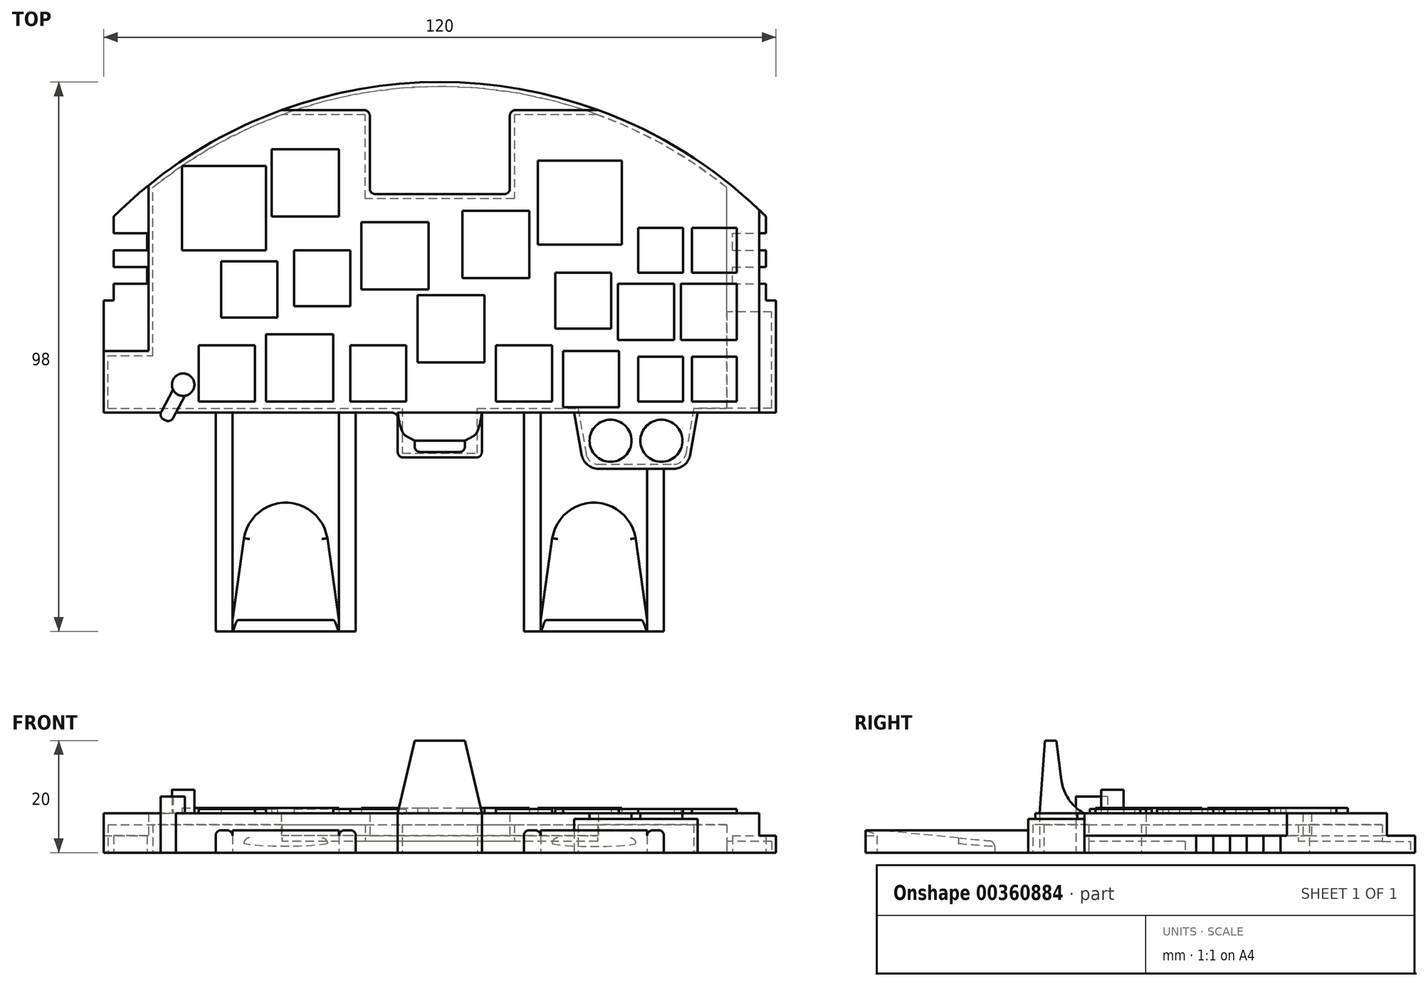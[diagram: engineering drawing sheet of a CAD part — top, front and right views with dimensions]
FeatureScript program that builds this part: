
annotation { "Feature Type Name" : "Feature", "Feature Type Description" : "" }
export const myFeature = defineFeature(function(context is Context, id is Id, definition is map)
    precondition{}
    {
        {
            var Q0;
            Q0=qCreatedBy(makeId("Top.planeOp"),FACE);
            var sketch = newSketch(context, id + "F0", { "sketchPlane" : qUnion([Q0])});
            skLineSegment(sketch, "E0", {"start": v(-60, 0) * mm, "end": v(60, 0) * mm});
            skLineSegment(sketch, "E1", {"start": v(60, 0) * mm, "end": v(60, 20) * mm});
            skLineSegment(sketch, "E2", {"start": v(60, 20) * mm, "end": v(58.2, 20) * mm});
            skLineSegment(sketch, "E3", {"start": v(58.2, 20) * mm, "end": v(58.2, 35) * mm});
            skLineSegment(sketch, "E4", {"start": v(-60, 0) * mm, "end": v(-60, 20) * mm});
            skLineSegment(sketch, "E5", {"start": v(-60, 20) * mm, "end": v(-58.2, 20) * mm});
            skLineSegment(sketch, "E6", {"start": v(-58.2, 20) * mm, "end": v(-58.2, 35) * mm});
            skArc(sketch, "E7", {"start": v(58.2, 35) * mm, "mid": v(0, 59) * mm, "end": v(-58.2, 35) * mm});
            skPoint(sketch, "E8", {"position": v(0, 0) * mm});
            skPoint(sketch, "E9", {"position": v(0, 59) * mm});
            skSolve(sketch);
        }
        {
            var Q0;
            Q0 = qSketchRegion(id + "F0", true);
            extrude(context, id + "F1", {"entities" : qUnion([Q0]), "depth" : 3 * mm});
        }
        {
            var Q0;
            Q0=makeQuery(id+"F1.opExtrude","CAP_FACE",FACE,{"disambiguationData":[OSD([sQuery(id+"F0.wireOp",EDGE,"E0"),sQuery(id+"F0.wireOp",EDGE,"E1"),sQuery(id+"F0.wireOp",EDGE,"E2"),sQuery(id+"F0.wireOp",EDGE,"E3"),sQuery(id+"F0.wireOp",EDGE,"E4"),sQuery(id+"F0.wireOp",EDGE,"E5"),sQuery(id+"F0.wireOp",EDGE,"E6"),sQuery(id+"F0.wireOp",EDGE,"E7")])],"isStart":false});
            var sketch = newSketch(context, id + "F2", { "sketchPlane" : qUnion([Q0])});
            skLineSegment(sketch, "E10", {"start": v(-60, 0) * mm, "end": v(57, 0) * mm});
            skLineSegment(sketch, "E11", {"start": v(57, 0) * mm, "end": v(57, 36.17) * mm});
            skLineSegment(sketch, "E12", {"start": v(-60, 0) * mm, "end": v(-60, 11) * mm});
            skLineSegment(sketch, "E13", {"start": v(-60, 11) * mm, "end": v(-52, 11) * mm});
            skLineSegment(sketch, "E14", {"start": v(-52, 11) * mm, "end": v(-52, 40.57) * mm});
            skArc(sketch, "E15", {"start": v(57, 36.17) * mm, "mid": v(43.57, 46.57) * mm, "end": v(28.3, 54) * mm});
            skLineSegment(sketch, "E16", {"start": v(-12.5, 39) * mm, "end": v(12.5, 39) * mm});
            skLineSegment(sketch, "E17", {"start": v(12.5, 39) * mm, "end": v(12.5, 54) * mm});
            skLineSegment(sketch, "E18", {"start": v(-12.5, 39) * mm, "end": v(-12.5, 54) * mm});
            skPoint(sketch, "E19", {"position": v(0, 39) * mm});
            skLineSegment(sketch, "E20", {"start": v(12.5, 54) * mm, "end": v(28.3, 54) * mm});
            skLineSegment(sketch, "E21", {"start": v(-12.5, 54) * mm, "end": v(-28.3, 54) * mm});
            skArc(sketch, "E22.trimOffspring", {"start": v(-28.3, 54) * mm, "mid": v(-40.7, 48.27) * mm, "end": v(-52, 40.57) * mm});
            skSolve(sketch);
        }
        {
            var Q0;
            Q0 = qSketchRegion(id + "F2", true);
            extrude(context, id + "F3", {"entities" : qUnion([Q0]), "operationType" : NewBodyOperationType.ADD, "depth" : 4 * mm});
        }
        {
            var Q0;
            Q0=makeQuery(id+"F3.opExtrude","CAP_FACE",FACE,{"disambiguationData":[OSD([sQuery(id+"F2.wireOp",EDGE,"E10"),sQuery(id+"F2.wireOp",EDGE,"E11"),sQuery(id+"F2.wireOp",EDGE,"E12"),sQuery(id+"F2.wireOp",EDGE,"E13"),sQuery(id+"F2.wireOp",EDGE,"E14"),sQuery(id+"F2.wireOp",EDGE,"E15"),sQuery(id+"F2.wireOp",EDGE,"E16"),sQuery(id+"F2.wireOp",EDGE,"E17"),sQuery(id+"F2.wireOp",EDGE,"E18"),sQuery(id+"F2.wireOp",EDGE,"E20"),sQuery(id+"F2.wireOp",EDGE,"E21"),sQuery(id+"F2.wireOp",EDGE,"E22.trimOffspring")])],"isStart":false});
            var sketch = newSketch(context, id + "F4", { "sketchPlane" : qUnion([Q0])});
            skLineSegment(sketch, "E23.bottom", {"start": v(17.5, 45) * mm, "end": v(32.5, 45) * mm});
            skLineSegment(sketch, "E23.top", {"start": v(17.5, 30) * mm, "end": v(32.5, 30) * mm});
            skLineSegment(sketch, "E23.left", {"start": v(17.5, 45) * mm, "end": v(17.5, 30) * mm});
            skLineSegment(sketch, "E23.right", {"start": v(32.5, 45) * mm, "end": v(32.5, 30) * mm});
            skLineSegment(sketch, "E24.bottom", {"start": v(-46, 44) * mm, "end": v(-31, 44) * mm});
            skLineSegment(sketch, "E24.top", {"start": v(-46, 29) * mm, "end": v(-31, 29) * mm});
            skLineSegment(sketch, "E24.left", {"start": v(-46, 44) * mm, "end": v(-46, 29) * mm});
            skLineSegment(sketch, "E24.right", {"start": v(-31, 44) * mm, "end": v(-31, 29) * mm});
            skSolve(sketch);
        }
        {
            var Q0;
            Q0 = qSketchRegion(id + "F4", true);
            extrude(context, id + "F5", {"entities" : qUnion([Q0]), "operationType" : NewBodyOperationType.ADD, "depth" : 1 * mm});
        }
        {
            var Q0;
            Q0=makeQuery(id+"F3.opExtrude","CAP_FACE",FACE,{"disambiguationData":[OSD([sQuery(id+"F2.wireOp",EDGE,"E10"),sQuery(id+"F2.wireOp",EDGE,"E11"),sQuery(id+"F2.wireOp",EDGE,"E12"),sQuery(id+"F2.wireOp",EDGE,"E13"),sQuery(id+"F2.wireOp",EDGE,"E14"),sQuery(id+"F2.wireOp",EDGE,"E15"),sQuery(id+"F2.wireOp",EDGE,"E16"),sQuery(id+"F2.wireOp",EDGE,"E17"),sQuery(id+"F2.wireOp",EDGE,"E18"),sQuery(id+"F2.wireOp",EDGE,"E20"),sQuery(id+"F2.wireOp",EDGE,"E21"),sQuery(id+"F2.wireOp",EDGE,"E22.trimOffspring")])],"isStart":false});
            var sketch = newSketch(context, id + "F6", { "sketchPlane" : qUnion([Q0])});
            skLineSegment(sketch, "E25.bottom", {"start": v(-30, 47) * mm, "end": v(-18, 47) * mm});
            skLineSegment(sketch, "E25.top", {"start": v(-30, 35) * mm, "end": v(-18, 35) * mm});
            skLineSegment(sketch, "E25.left", {"start": v(-30, 47) * mm, "end": v(-30, 35) * mm});
            skLineSegment(sketch, "E25.right", {"start": v(-18, 47) * mm, "end": v(-18, 35) * mm});
            skLineSegment(sketch, "E26.bottom", {"start": v(-14, 34) * mm, "end": v(-2, 34) * mm});
            skLineSegment(sketch, "E26.top", {"start": v(-14, 22) * mm, "end": v(-2, 22) * mm});
            skLineSegment(sketch, "E26.left", {"start": v(-14, 34) * mm, "end": v(-14, 22) * mm});
            skLineSegment(sketch, "E26.right", {"start": v(-2, 34) * mm, "end": v(-2, 22) * mm});
            skLineSegment(sketch, "E27.bottom", {"start": v(4, 36) * mm, "end": v(16, 36) * mm});
            skLineSegment(sketch, "E27.top", {"start": v(4, 24) * mm, "end": v(16, 24) * mm});
            skLineSegment(sketch, "E27.left", {"start": v(4, 36) * mm, "end": v(4, 24) * mm});
            skLineSegment(sketch, "E27.right", {"start": v(16, 36) * mm, "end": v(16, 24) * mm});
            skLineSegment(sketch, "E28.bottom", {"start": v(-4, 21) * mm, "end": v(8, 21) * mm});
            skLineSegment(sketch, "E28.top", {"start": v(-4, 9) * mm, "end": v(8, 9) * mm});
            skLineSegment(sketch, "E28.left", {"start": v(-4, 21) * mm, "end": v(-4, 9) * mm});
            skLineSegment(sketch, "E28.right", {"start": v(8, 21) * mm, "end": v(8, 9) * mm});
            skLineSegment(sketch, "E29.bottom", {"start": v(-31, 14) * mm, "end": v(-19, 14) * mm});
            skLineSegment(sketch, "E29.top", {"start": v(-31, 2) * mm, "end": v(-19, 2) * mm});
            skLineSegment(sketch, "E29.left", {"start": v(-31, 14) * mm, "end": v(-31, 2) * mm});
            skLineSegment(sketch, "E29.right", {"start": v(-19, 14) * mm, "end": v(-19, 2) * mm});
            skSolve(sketch);
        }
        {
            var Q0;
            Q0 = qSketchRegion(id + "F6", true);
            extrude(context, id + "F7", {"entities" : qUnion([Q0]), "operationType" : NewBodyOperationType.ADD, "depth" : 1 * mm});
        }
        {
            var Q0;
            Q0=makeQuery(id+"F3.opExtrude","CAP_FACE",FACE,{"disambiguationData":[OSD([sQuery(id+"F2.wireOp",EDGE,"E10"),sQuery(id+"F2.wireOp",EDGE,"E11"),sQuery(id+"F2.wireOp",EDGE,"E12"),sQuery(id+"F2.wireOp",EDGE,"E13"),sQuery(id+"F2.wireOp",EDGE,"E14"),sQuery(id+"F2.wireOp",EDGE,"E15"),sQuery(id+"F2.wireOp",EDGE,"E16"),sQuery(id+"F2.wireOp",EDGE,"E17"),sQuery(id+"F2.wireOp",EDGE,"E18"),sQuery(id+"F2.wireOp",EDGE,"E20"),sQuery(id+"F2.wireOp",EDGE,"E21"),sQuery(id+"F2.wireOp",EDGE,"E22.trimOffspring")])],"isStart":false});
            var sketch = newSketch(context, id + "F8", { "sketchPlane" : qUnion([Q0])});
            skLineSegment(sketch, "E30.bottom", {"start": v(-39, 27) * mm, "end": v(-29, 27) * mm});
            skLineSegment(sketch, "E30.top", {"start": v(-39, 17) * mm, "end": v(-29, 17) * mm});
            skLineSegment(sketch, "E30.left", {"start": v(-39, 27) * mm, "end": v(-39, 17) * mm});
            skLineSegment(sketch, "E30.right", {"start": v(-29, 27) * mm, "end": v(-29, 17) * mm});
            skLineSegment(sketch, "E31.bottom", {"start": v(-26, 29) * mm, "end": v(-16, 29) * mm});
            skLineSegment(sketch, "E31.top", {"start": v(-26, 19) * mm, "end": v(-16, 19) * mm});
            skLineSegment(sketch, "E31.left", {"start": v(-26, 29) * mm, "end": v(-26, 19) * mm});
            skLineSegment(sketch, "E31.right", {"start": v(-16, 29) * mm, "end": v(-16, 19) * mm});
            skLineSegment(sketch, "E32.bottom", {"start": v(-16, 12) * mm, "end": v(-6, 12) * mm});
            skLineSegment(sketch, "E32.top", {"start": v(-16, 2) * mm, "end": v(-6, 2) * mm});
            skLineSegment(sketch, "E32.left", {"start": v(-16, 12) * mm, "end": v(-16, 2) * mm});
            skLineSegment(sketch, "E32.right", {"start": v(-6, 12) * mm, "end": v(-6, 2) * mm});
            skLineSegment(sketch, "E33.bottom", {"start": v(10, 12) * mm, "end": v(20, 12) * mm});
            skLineSegment(sketch, "E33.top", {"start": v(10, 2) * mm, "end": v(20, 2) * mm});
            skLineSegment(sketch, "E33.left", {"start": v(10, 12) * mm, "end": v(10, 2) * mm});
            skLineSegment(sketch, "E33.right", {"start": v(20, 12) * mm, "end": v(20, 2) * mm});
            skLineSegment(sketch, "E34.bottom", {"start": v(22, 11) * mm, "end": v(32, 11) * mm});
            skLineSegment(sketch, "E34.top", {"start": v(22, 1) * mm, "end": v(32, 1) * mm});
            skLineSegment(sketch, "E34.left", {"start": v(22, 11) * mm, "end": v(22, 1) * mm});
            skLineSegment(sketch, "E34.right", {"start": v(32, 11) * mm, "end": v(32, 1) * mm});
            skLineSegment(sketch, "E35.bottom", {"start": v(20.6, 25) * mm, "end": v(30.6, 25) * mm});
            skLineSegment(sketch, "E35.top", {"start": v(20.6, 15) * mm, "end": v(30.6, 15) * mm});
            skLineSegment(sketch, "E35.left", {"start": v(20.6, 25) * mm, "end": v(20.6, 15) * mm});
            skLineSegment(sketch, "E35.right", {"start": v(30.6, 25) * mm, "end": v(30.6, 15) * mm});
            skLineSegment(sketch, "E36.bottom", {"start": v(31.8, 23) * mm, "end": v(41.8, 23) * mm});
            skLineSegment(sketch, "E36.top", {"start": v(31.8, 13) * mm, "end": v(41.8, 13) * mm});
            skLineSegment(sketch, "E36.left", {"start": v(31.8, 23) * mm, "end": v(31.8, 13) * mm});
            skLineSegment(sketch, "E36.right", {"start": v(41.8, 23) * mm, "end": v(41.8, 13) * mm});
            skLineSegment(sketch, "E37.bottom", {"start": v(43, 23) * mm, "end": v(53, 23) * mm});
            skLineSegment(sketch, "E37.top", {"start": v(43, 13) * mm, "end": v(53, 13) * mm});
            skLineSegment(sketch, "E37.left", {"start": v(43, 23) * mm, "end": v(43, 13) * mm});
            skLineSegment(sketch, "E37.right", {"start": v(53, 23) * mm, "end": v(53, 13) * mm});
            skLineSegment(sketch, "E38.bottom", {"start": v(-43, 12) * mm, "end": v(-33, 12) * mm});
            skLineSegment(sketch, "E38.top", {"start": v(-43, 2) * mm, "end": v(-33, 2) * mm});
            skLineSegment(sketch, "E38.left", {"start": v(-43, 12) * mm, "end": v(-43, 2) * mm});
            skLineSegment(sketch, "E38.right", {"start": v(-33, 12) * mm, "end": v(-33, 2) * mm});
            skSolve(sketch);
        }
        {
            var Q0;
            Q0 = qSketchRegion(id + "F8", true);
            extrude(context, id + "F9", {"entities" : qUnion([Q0]), "operationType" : NewBodyOperationType.ADD, "depth" : 0.8 * mm});
        }
        {
            var Q0;
            Q0=makeQuery(id+"F3.opExtrude","CAP_FACE",FACE,{"disambiguationData":[OSD([sQuery(id+"F2.wireOp",EDGE,"E10"),sQuery(id+"F2.wireOp",EDGE,"E11"),sQuery(id+"F2.wireOp",EDGE,"E12"),sQuery(id+"F2.wireOp",EDGE,"E13"),sQuery(id+"F2.wireOp",EDGE,"E14"),sQuery(id+"F2.wireOp",EDGE,"E15"),sQuery(id+"F2.wireOp",EDGE,"E16"),sQuery(id+"F2.wireOp",EDGE,"E17"),sQuery(id+"F2.wireOp",EDGE,"E18"),sQuery(id+"F2.wireOp",EDGE,"E20"),sQuery(id+"F2.wireOp",EDGE,"E21"),sQuery(id+"F2.wireOp",EDGE,"E22.trimOffspring")])],"isStart":false});
            var sketch = newSketch(context, id + "F10", { "sketchPlane" : qUnion([Q0])});
            skLineSegment(sketch, "E39.bottom", {"start": v(35.4, 10) * mm, "end": v(43.4, 10) * mm});
            skLineSegment(sketch, "E39.top", {"start": v(35.4, 2) * mm, "end": v(43.4, 2) * mm});
            skLineSegment(sketch, "E39.left", {"start": v(35.4, 10) * mm, "end": v(35.4, 2) * mm});
            skLineSegment(sketch, "E39.right", {"start": v(43.4, 10) * mm, "end": v(43.4, 2) * mm});
            skLineSegment(sketch, "E40.bottom", {"start": v(45, 10) * mm, "end": v(53, 10) * mm});
            skLineSegment(sketch, "E40.top", {"start": v(45, 2) * mm, "end": v(53, 2) * mm});
            skLineSegment(sketch, "E40.left", {"start": v(45, 10) * mm, "end": v(45, 2) * mm});
            skLineSegment(sketch, "E40.right", {"start": v(53, 10) * mm, "end": v(53, 2) * mm});
            skLineSegment(sketch, "E41.bottom", {"start": v(35.4, 33) * mm, "end": v(43.4, 33) * mm});
            skLineSegment(sketch, "E41.top", {"start": v(35.4, 25) * mm, "end": v(43.4, 25) * mm});
            skLineSegment(sketch, "E41.left", {"start": v(35.4, 33) * mm, "end": v(35.4, 25) * mm});
            skLineSegment(sketch, "E41.right", {"start": v(43.4, 33) * mm, "end": v(43.4, 25) * mm});
            skLineSegment(sketch, "E42.bottom", {"start": v(45, 33) * mm, "end": v(53, 33) * mm});
            skLineSegment(sketch, "E42.top", {"start": v(45, 25) * mm, "end": v(53, 25) * mm});
            skLineSegment(sketch, "E42.left", {"start": v(45, 33) * mm, "end": v(45, 25) * mm});
            skLineSegment(sketch, "E42.right", {"start": v(53, 33) * mm, "end": v(53, 25) * mm});
            skSolve(sketch);
        }
        {
            var Q0;
            Q0 = qSketchRegion(id + "F10", true);
            extrude(context, id + "F11", {"entities" : qUnion([Q0]), "operationType" : NewBodyOperationType.ADD, "depth" : 0.8 * mm});
        }
        {
            var Q0;
            Q0=qCreatedBy(makeId("Top.planeOp"),FACE);
            var sketch = newSketch(context, id + "F12", { "sketchPlane" : qUnion([Q0])});
            skCircle(sketch, "E43", {"center": v(-45.8, 5) * mm, "radius": 2 * mm});
            skLineSegment(sketch, "E44", {"start": v(-47.61, 4.15) * mm, "end": v(-50.19, -0.7) * mm});
            skLineSegment(sketch, "E45", {"start": v(-50.19, -0.7) * mm, "end": v(-48.07, -1.83) * mm});
            skLineSegment(sketch, "E46", {"start": v(-48.07, -1.83) * mm, "end": v(-45.5, 3.02) * mm});
            skSolve(sketch);
        }
        {
            var Q0;
            Q0 = qSketchRegion(id + "F12", true);
            extrude(context, id + "F13", {"entities" : qUnion([Q0]), "operationType" : NewBodyOperationType.ADD, "depth" : 10 * mm});
        }
        {
            var Q0;
            Q0=makeQuery(id+"F13.opExtrude","CAP_FACE",FACE,{"disambiguationData":[OSD([sQuery(id+"F12.wireOp",EDGE,"E43"),sQuery(id+"F12.wireOp",EDGE,"E44"),sQuery(id+"F12.wireOp",EDGE,"E45"),sQuery(id+"F12.wireOp",EDGE,"E46")])],"isStart":false});
            var sketch = newSketch(context, id + "F14", { "sketchPlane" : qUnion([Q0])});
            skCircle(sketch, "E47", {"center": v(-45.8, 5) * mm, "radius": 2 * mm});
            skSolve(sketch);
        }
        {
            var Q0;
            Q0 = qSketchRegion(id + "F14", true);
            extrude(context, id + "F15", {"entities" : qUnion([Q0]), "operationType" : NewBodyOperationType.ADD, "depth" : 1.2 * mm});
        }
        {
            var Q0;
            Q0=qCreatedBy(makeId("Top.planeOp"),FACE);
            var sketch = newSketch(context, id + "F16", { "sketchPlane" : qUnion([Q0])});
            skLineSegment(sketch, "E48", {"start": v(44.67, -7.52) * mm, "end": v(46, 0) * mm});
            skLineSegment(sketch, "E49", {"start": v(25.33, -7.52) * mm, "end": v(24, 0) * mm});
            skLineSegment(sketch, "E50", {"start": v(28.28, -10) * mm, "end": v(41.72, -10) * mm});
            skArc(sketch, "E51", {"start": v(25.33, -7.52) * mm, "mid": v(26.35, -9.3) * mm, "end": v(28.28, -10) * mm});
            skArc(sketch, "E52", {"start": v(44.67, -7.52) * mm, "mid": v(43.65, -9.3) * mm, "end": v(41.72, -10) * mm});
            skLineSegment(sketch, "E53", {"start": v(24, 0) * mm, "end": v(46, 0) * mm});
            skCircle(sketch, "E54", {"center": v(30.47, -5) * mm, "radius": 3.75 * mm});
            skCircle(sketch, "E55", {"center": v(39.53, -5) * mm, "radius": 3.75 * mm});
            skSolve(sketch);
        }
        {
            var Q0;
            Q0 = qSketchRegion(id + "F16", true);
            var Q1;
            Q1=makeQuery(id+"F16.imprint","IMPRINT",FACE,{"disambiguationData":[TD([[makeQuery(id+"F16.imprint","IMPRINT",EDGE,{"derivedFrom":sQuery(id+"F16.wireOp",EDGE,"E54")}),1.0]])]});
            var Q2;
            Q2=makeQuery(id+"F16.imprint","IMPRINT",FACE,{"disambiguationData":[TD([[makeQuery(id+"F16.imprint","IMPRINT",EDGE,{"derivedFrom":sQuery(id+"F16.wireOp",EDGE,"E55")}),1.0]])]});
            extrude(context, id + "F17", {"entities" : qUnion([Q0, Q1, Q2]), "operationType" : NewBodyOperationType.ADD, "depth" : 6 * mm});
        }
        {
            var Q0;
            Q0=qCreatedBy(makeId("Front.planeOp"),FACE);
            var sketch = newSketch(context, id + "F18", { "sketchPlane" : qUnion([Q0])});
            skLineSegment(sketch, "E56.bottom", {"start": v(-40, 4) * mm, "end": v(-37, 4) * mm});
            skLineSegment(sketch, "E56.top", {"start": v(-40, 0) * mm, "end": v(-37, 0) * mm});
            skLineSegment(sketch, "E56.left", {"start": v(-40, 4) * mm, "end": v(-40, 0) * mm});
            skLineSegment(sketch, "E56.right", {"start": v(-37, 4) * mm, "end": v(-37, 0) * mm});
            skLineSegment(sketch, "E57.bottom", {"start": v(-18, 4) * mm, "end": v(-15, 4) * mm});
            skLineSegment(sketch, "E57.top", {"start": v(-18, 0) * mm, "end": v(-15, 0) * mm});
            skLineSegment(sketch, "E57.left", {"start": v(-18, 4) * mm, "end": v(-18, 0) * mm});
            skLineSegment(sketch, "E57.right", {"start": v(-15, 4) * mm, "end": v(-15, 0) * mm});
            skLineSegment(sketch, "E58.bottom", {"start": v(15, 4) * mm, "end": v(18, 4) * mm});
            skLineSegment(sketch, "E58.top", {"start": v(15, 0) * mm, "end": v(18, 0) * mm});
            skLineSegment(sketch, "E58.left", {"start": v(15, 4) * mm, "end": v(15, 0) * mm});
            skLineSegment(sketch, "E58.right", {"start": v(18, 4) * mm, "end": v(18, 0) * mm});
            skLineSegment(sketch, "E59.bottom", {"start": v(37, 4) * mm, "end": v(40, 4) * mm});
            skLineSegment(sketch, "E59.top", {"start": v(37, 0) * mm, "end": v(40, 0) * mm});
            skLineSegment(sketch, "E59.left", {"start": v(37, 4) * mm, "end": v(37, 0) * mm});
            skLineSegment(sketch, "E59.right", {"start": v(40, 4) * mm, "end": v(40, 0) * mm});
            skSolve(sketch);
        }
        {
            var Q0;
            Q0 = qSketchRegion(id + "F18", true);
            extrude(context, id + "F19", {"entities" : qUnion([Q0]), "operationType" : NewBodyOperationType.ADD, "depth" : 39 * mm});
        }
        {
            var Q0;
            Q0=qCreatedBy(makeId("Top.planeOp"),FACE);
            var sketch = newSketch(context, id + "F20", { "sketchPlane" : qUnion([Q0])});
            skLineSegment(sketch, "E60.bottom", {"start": v(-7.5, 0) * mm, "end": v(7.5, 0) * mm});
            skLineSegment(sketch, "E60.top", {"start": v(-7.5, -8) * mm, "end": v(7.5, -8) * mm});
            skLineSegment(sketch, "E60.left", {"start": v(-7.5, 0) * mm, "end": v(-7.5, -8) * mm});
            skLineSegment(sketch, "E60.right", {"start": v(7.5, 0) * mm, "end": v(7.5, -8) * mm});
            skPoint(sketch, "E61", {"position": v(0, -8) * mm});
            skSolve(sketch);
        }
        {
            var Q0;
            Q0 = qSketchRegion(id + "F20", true);
            extrude(context, id + "F21", {"entities" : qUnion([Q0]), "operationType" : NewBodyOperationType.ADD, "depth" : 7 * mm});
        }
        {
            var Q0;
            Q0=qCreatedBy(makeId("Top.planeOp"),FACE);
            cPlane(context, id + "F22", {"entities" : qUnion([Q0]), "cplaneType" : CPlaneType.OFFSET, "offset" : 20 * mm, "width" : 150 * mm, "height" : 150 * mm});
        }
        {
            var Q0;
            Q0=qCreatedBy(id+"F22.planeOp",FACE);
            var sketch = newSketch(context, id + "F23", { "sketchPlane" : qUnion([Q0])});
            skLineSegment(sketch, "E62.bottom", {"start": v(-4.5, -1) * mm, "end": v(4.5, -1) * mm});
            skLineSegment(sketch, "E62.top", {"start": v(-4.5, -7) * mm, "end": v(4.5, -7) * mm});
            skLineSegment(sketch, "E62.left", {"start": v(-4.5, -1) * mm, "end": v(-4.5, -7) * mm});
            skLineSegment(sketch, "E62.right", {"start": v(4.5, -1) * mm, "end": v(4.5, -7) * mm});
            skPoint(sketch, "E63", {"position": v(0, -7) * mm});
            skSolve(sketch);
        }
        {
            var Q0;
            Q0=makeQuery(id+"F21.boolean.opBoolean","MERGE",FACE,{"derivedFrom":[makeQuery(id+"F3.opExtrude","CAP_FACE",FACE,{"disambiguationData":[OSD([sQuery(id+"F2.wireOp",EDGE,"E10"),sQuery(id+"F2.wireOp",EDGE,"E11"),sQuery(id+"F2.wireOp",EDGE,"E12"),sQuery(id+"F2.wireOp",EDGE,"E13"),sQuery(id+"F2.wireOp",EDGE,"E14"),sQuery(id+"F2.wireOp",EDGE,"E15"),sQuery(id+"F2.wireOp",EDGE,"E16"),sQuery(id+"F2.wireOp",EDGE,"E17"),sQuery(id+"F2.wireOp",EDGE,"E18"),sQuery(id+"F2.wireOp",EDGE,"E20"),sQuery(id+"F2.wireOp",EDGE,"E21"),sQuery(id+"F2.wireOp",EDGE,"E22.trimOffspring")])],"isStart":false}),makeQuery(id+"F21.opExtrude","CAP_FACE",FACE,{"disambiguationData":[OSD([sQuery(id+"F20.wireOp",EDGE,"E60.bottom"),sQuery(id+"F20.wireOp",EDGE,"E60.top"),sQuery(id+"F20.wireOp",EDGE,"E60.left"),sQuery(id+"F20.wireOp",EDGE,"E60.right")])],"isStart":false})]});
            var sketch = newSketch(context, id + "F24", { "sketchPlane" : qUnion([Q0])});
            skLineSegment(sketch, "E64.bottom", {"start": v(-7.5, -8) * mm, "end": v(7.5, -8) * mm});
            skLineSegment(sketch, "E64.top", {"start": v(-7.5, 0) * mm, "end": v(7.5, 0) * mm});
            skLineSegment(sketch, "E64.left", {"start": v(-7.5, -8) * mm, "end": v(-7.5, 0) * mm});
            skLineSegment(sketch, "E64.right", {"start": v(7.5, -8) * mm, "end": v(7.5, 0) * mm});
            skSolve(sketch);
        }
        {
            var Q1;
            Q1=makeQuery(id+"F24.imprint","IMPRINT",FACE,{"disambiguationData":[TD([[makeQuery(id+"F24.imprint","IMPRINT",EDGE,{"derivedFrom":sQuery(id+"F24.wireOp",EDGE,"E64.bottom")}),1.0]])]});
            var Q2;
            Q2=makeQuery(id+"F23.imprint","IMPRINT",FACE,{"disambiguationData":[TD([[makeQuery(id+"F23.imprint","IMPRINT",EDGE,{"derivedFrom":sQuery(id+"F23.wireOp",EDGE,"E62.bottom")}),-1.0]])]});
            loft(context, id + "F25", {"operationType" : NewBodyOperationType.ADD, "sheetProfilesArray" : [{ "sheetProfileEntities" : qUnion([Q1]) }, { "sheetProfileEntities" : qUnion([Q2]) }]});
        }
        {
            var Q0;
            Q0=qCreatedBy(makeId("Right.planeOp"),FACE);
            var sketch = newSketch(context, id + "F26", { "sketchPlane" : qUnion([Q0])});
            skLineSegment(sketch, "E65", {"start": v(-5, 20) * mm, "end": v(-4.1, 13) * mm});
            skArc(sketch, "E66", {"start": v(-4.1, 13) * mm, "mid": v(-2.77, 9.5) * mm, "end": v(0, 7) * mm});
            skLineSegment(sketch, "E67", {"start": v(-5, 20) * mm, "end": v(0, 20) * mm});
            skLineSegment(sketch, "E68", {"start": v(0, 20) * mm, "end": v(0, 7) * mm});
            skSolve(sketch);
        }
        {
            var Q0;
            Q0 = qSketchRegion(id + "F26", true);
            extrude(context, id + "F27", {"entities" : qUnion([Q0]), "operationType" : NewBodyOperationType.REMOVE, "endBound" : BoundingType.SYMMETRIC, "oppositeDirection" : true, "depth" : 25 * mm});
        }
        {
            var Q0;
            Q0=makeQuery(id+"F16.imprint","IMPRINT",FACE,{"disambiguationData":[TD([[makeQuery(id+"F16.imprint","IMPRINT",EDGE,{"derivedFrom":sQuery(id+"F16.wireOp",EDGE,"E55")}),1.0]])]});
            var Q1;
            Q1=makeQuery(id+"F16.imprint","IMPRINT",FACE,{"disambiguationData":[TD([[makeQuery(id+"F16.imprint","IMPRINT",EDGE,{"derivedFrom":sQuery(id+"F16.wireOp",EDGE,"E54")}),1.0]])]});
            extrude(context, id + "F28", {"entities" : qUnion([Q0, Q1]), "operationType" : NewBodyOperationType.ADD, "depth" : 7 * mm});
        }
        {
            var Q0;
            Q0=makeQuery(id+"F19.opExtrude","SWEPT_EDGE",EDGE,{"disambiguationData":[OSD([sQuery(id+"F18.wireOp",EDGE,"E56.bottom"),sQuery(id+"F18.wireOp",EDGE,"E56.left")])]});
            var Q1;
            Q1=makeQuery(id+"F19.opExtrude","SWEPT_EDGE",EDGE,{"disambiguationData":[OSD([sQuery(id+"F18.wireOp",EDGE,"E56.bottom"),sQuery(id+"F18.wireOp",EDGE,"E56.right")])]});
            var Q2;
            Q2=makeQuery(id+"F19.opExtrude","SWEPT_EDGE",EDGE,{"disambiguationData":[OSD([sQuery(id+"F18.wireOp",EDGE,"E57.bottom"),sQuery(id+"F18.wireOp",EDGE,"E57.left")])]});
            var Q3;
            Q3=makeQuery(id+"F19.opExtrude","SWEPT_EDGE",EDGE,{"disambiguationData":[OSD([sQuery(id+"F18.wireOp",EDGE,"E57.bottom"),sQuery(id+"F18.wireOp",EDGE,"E57.right")])]});
            var Q4;
            Q4=makeQuery(id+"F19.opExtrude","SWEPT_EDGE",EDGE,{"disambiguationData":[OSD([sQuery(id+"F18.wireOp",EDGE,"E58.bottom"),sQuery(id+"F18.wireOp",EDGE,"E58.left")])]});
            var Q5;
            Q5=makeQuery(id+"F19.opExtrude","SWEPT_EDGE",EDGE,{"disambiguationData":[OSD([sQuery(id+"F18.wireOp",EDGE,"E58.bottom"),sQuery(id+"F18.wireOp",EDGE,"E58.right")])]});
            var Q6;
            Q6=makeQuery(id+"F19.opExtrude","SWEPT_EDGE",EDGE,{"disambiguationData":[OSD([sQuery(id+"F18.wireOp",EDGE,"E59.bottom"),sQuery(id+"F18.wireOp",EDGE,"E59.left")])]});
            var Q7;
            Q7=makeQuery(id+"F19.opExtrude","SWEPT_EDGE",EDGE,{"disambiguationData":[OSD([sQuery(id+"F18.wireOp",EDGE,"E59.bottom"),sQuery(id+"F18.wireOp",EDGE,"E59.right")])]});
            var Q8;
            Q8=makeQuery(id+"F3.opExtrude","SWEPT_EDGE",EDGE,{"disambiguationData":[OSD([sQuery(id+"F2.wireOp",EDGE,"E18"),sQuery(id+"F2.wireOp",EDGE,"E21")])]});
            var Q9;
            Q9=makeQuery(id+"F3.opExtrude","SWEPT_EDGE",EDGE,{"disambiguationData":[OSD([sQuery(id+"F2.wireOp",EDGE,"E17"),sQuery(id+"F2.wireOp",EDGE,"E20")])]});
            var Q10;
            Q10=makeQuery(id+"F3.opExtrude","SWEPT_EDGE",EDGE,{"disambiguationData":[OSD([sQuery(id+"F2.wireOp",EDGE,"E16"),sQuery(id+"F2.wireOp",EDGE,"E18")])]});
            var Q11;
            Q11=makeQuery(id+"F3.opExtrude","SWEPT_EDGE",EDGE,{"disambiguationData":[OSD([sQuery(id+"F2.wireOp",EDGE,"E16"),sQuery(id+"F2.wireOp",EDGE,"E17")])]});
            var Q12;
            Q12=makeQuery(id+"F13.opExtrude","SWEPT_EDGE",EDGE,{"disambiguationData":[OSD([sQuery(id+"F12.wireOp",EDGE,"E44"),sQuery(id+"F12.wireOp",EDGE,"E45")])]});
            var Q13;
            Q13=makeQuery(id+"F13.opExtrude","SWEPT_EDGE",EDGE,{"disambiguationData":[OSD([sQuery(id+"F12.wireOp",EDGE,"E45"),sQuery(id+"F12.wireOp",EDGE,"E46")])]});
            var Q14;
            Q14=makeQuery(id+"F21.opExtrude","SWEPT_EDGE",EDGE,{"disambiguationData":[OSD([sQuery(id+"F20.wireOp",EDGE,"E60.top"),sQuery(id+"F20.wireOp",EDGE,"E60.left")])]});
            var Q15;
            Q15=makeQuery(id+"F21.opExtrude","SWEPT_EDGE",EDGE,{"disambiguationData":[OSD([sQuery(id+"F20.wireOp",EDGE,"E60.bottom"),sQuery(id+"F20.wireOp",EDGE,"E60.left")])]});
            var Q16;
            Q16=makeQuery(id+"F21.opExtrude","SWEPT_EDGE",EDGE,{"disambiguationData":[OSD([sQuery(id+"F20.wireOp",EDGE,"E60.top"),sQuery(id+"F20.wireOp",EDGE,"E60.right")])]});
            var Q17;
            Q17=makeQuery(id+"F21.opExtrude","SWEPT_EDGE",EDGE,{"disambiguationData":[OSD([sQuery(id+"F20.wireOp",EDGE,"E60.bottom"),sQuery(id+"F20.wireOp",EDGE,"E60.right")])]});
            fillet(context, id + "F29", {"entities" : qUnion([Q0, Q1, Q2, Q3, Q4, Q5, Q6, Q7, Q8, Q9, Q10, Q11, Q12, Q13, Q14, Q15, Q16, Q17]), "radius" : 1 * mm, "tangentPropagation" : true, "allowEdgeOverflow" : false});
        }
        {
            var Q0;
            Q0=qCreatedBy(makeId("Top.planeOp"),FACE);
            var sketch = newSketch(context, id + "F30", { "sketchPlane" : qUnion([Q0])});
            skLineSegment(sketch, "E69", {"start": v(-37, -39) * mm, "end": v(-18, -39) * mm});
            skLineSegment(sketch, "E70", {"start": v(-18, -39) * mm, "end": v(-18, -37) * mm});
            skLineSegment(sketch, "E71", {"start": v(-18, -37) * mm, "end": v(-20.04, -22.48) * mm});
            skLineSegment(sketch, "E72", {"start": v(-37, -39) * mm, "end": v(-37, -37) * mm});
            skLineSegment(sketch, "E73", {"start": v(-37, -37) * mm, "end": v(-34.96, -22.48) * mm});
            skArc(sketch, "E74", {"start": v(-34.96, -22.48) * mm, "mid": v(-27.5, -16) * mm, "end": v(-20.04, -22.48) * mm});
            skLineSegment(sketch, "E75", {"start": v(20.04, -22.48) * mm, "end": v(18, -37) * mm});
            skLineSegment(sketch, "E76", {"start": v(18, -37) * mm, "end": v(18, -39) * mm});
            skLineSegment(sketch, "E77", {"start": v(18, -39) * mm, "end": v(37, -39) * mm});
            skLineSegment(sketch, "E78", {"start": v(37, -39) * mm, "end": v(37, -37) * mm});
            skLineSegment(sketch, "E79", {"start": v(37, -37) * mm, "end": v(34.96, -22.48) * mm});
            skArc(sketch, "E80", {"start": v(20.04, -22.48) * mm, "mid": v(27.5, -16) * mm, "end": v(34.96, -22.48) * mm});
            skSolve(sketch);
        }
        {
            var Q0;
            Q0 = qSketchRegion(id + "F30", true);
            extrude(context, id + "F31", {"entities" : qUnion([Q0]), "operationType" : NewBodyOperationType.ADD, "depth" : 4 * mm});
        }
        {
            var Q0;
            Q0=qCreatedBy(makeId("Top.planeOp"),FACE);
            var sketch = newSketch(context, id + "F32", { "sketchPlane" : qUnion([Q0])});
            skLineSegment(sketch, "E81", {"start": v(-59.2, 0.8) * mm, "end": v(-6.7, 0.8) * mm});
            skLineSegment(sketch, "E82", {"start": v(-6.7, 0.8) * mm, "end": v(-6.7, -7.2) * mm});
            skLineSegment(sketch, "E83", {"start": v(-6.7, -7.2) * mm, "end": v(6.7, -7.2) * mm});
            skLineSegment(sketch, "E84", {"start": v(6.7, -7.2) * mm, "end": v(6.7, 0.8) * mm});
            skLineSegment(sketch, "E85", {"start": v(6.7, 0.8) * mm, "end": v(24.67, 0.8) * mm});
            skLineSegment(sketch, "E86", {"start": v(24.67, 0.8) * mm, "end": v(26.11, -7.38) * mm});
            skLineSegment(sketch, "E87", {"start": v(59.2, 0.8) * mm, "end": v(59.2, 18) * mm});
            skLineSegment(sketch, "E88", {"start": v(59.2, 18) * mm, "end": v(51.2, 18) * mm});
            skLineSegment(sketch, "E89", {"start": v(51.2, 18) * mm, "end": v(51.2, 40.19) * mm});
            skArc(sketch, "E90", {"start": v(51.2, 40.19) * mm, "mid": v(0, 58.2) * mm, "end": v(-51.2, 40.19) * mm});
            skLineSegment(sketch, "E91", {"start": v(28.28, -9.2) * mm, "end": v(41.72, -9.2) * mm});
            skArc(sketch, "E92", {"start": v(26.11, -7.38) * mm, "mid": v(26.87, -8.69) * mm, "end": v(28.28, -9.2) * mm});
            skLineSegment(sketch, "E93", {"start": v(59.2, 0.8) * mm, "end": v(45.33, 0.8) * mm});
            skLineSegment(sketch, "E94", {"start": v(45.33, 0.8) * mm, "end": v(43.89, -7.38) * mm});
            skArc(sketch, "E95", {"start": v(41.72, -9.2) * mm, "mid": v(43.13, -8.69) * mm, "end": v(43.89, -7.38) * mm});
            skLineSegment(sketch, "E96", {"start": v(-59.2, 0.8) * mm, "end": v(-59.2, 10.2) * mm});
            skLineSegment(sketch, "E97", {"start": v(-59.2, 10.2) * mm, "end": v(-51.2, 10.2) * mm});
            skLineSegment(sketch, "E98", {"start": v(-51.2, 10.2) * mm, "end": v(-51.2, 40.19) * mm});
            skSolve(sketch);
        }
        {
            var Q0;
            Q0 = qSketchRegion(id + "F32", true);
            extrude(context, id + "F33", {"entities" : qUnion([Q0]), "operationType" : NewBodyOperationType.REMOVE, "depth" : 2 * mm});
        }
        {
            var Q0;
            Q0=makeQuery(id+"F0.imprint","IMPRINT",FACE,{"disambiguationData":[TD([[makeQuery(id+"F0.imprint","IMPRINT",EDGE,{"derivedFrom":sQuery(id+"F0.wireOp",EDGE,"E0")}),1.0]])]});
            var sketch = newSketch(context, id + "F34", { "sketchPlane" : qUnion([Q0])});
            skLineSegment(sketch, "E99", {"start": v(-59.2, 0.8) * mm, "end": v(-6.7, 0.8) * mm});
            skLineSegment(sketch, "E100", {"start": v(-6.7, 0.8) * mm, "end": v(-6.7, -7.2) * mm});
            skLineSegment(sketch, "E101", {"start": v(-6.7, -7.2) * mm, "end": v(6.7, -7.2) * mm});
            skLineSegment(sketch, "E102", {"start": v(6.7, -7.2) * mm, "end": v(6.7, 0.8) * mm});
            skLineSegment(sketch, "E103", {"start": v(6.7, 0.8) * mm, "end": v(24.67, 0.8) * mm});
            skLineSegment(sketch, "E104", {"start": v(24.67, 0.8) * mm, "end": v(26.11, -7.38) * mm});
            skLineSegment(sketch, "E105", {"start": v(28.28, -9.2) * mm, "end": v(41.72, -9.2) * mm});
            skLineSegment(sketch, "E106", {"start": v(43.89, -7.38) * mm, "end": v(45.33, 0.8) * mm});
            skLineSegment(sketch, "E107", {"start": v(-28.15, 53.2) * mm, "end": v(-13.3, 53.2) * mm});
            skLineSegment(sketch, "E108", {"start": v(-13.3, 53.2) * mm, "end": v(-13.3, 38.2) * mm});
            skLineSegment(sketch, "E109", {"start": v(-13.3, 38.2) * mm, "end": v(13.3, 38.2) * mm});
            skLineSegment(sketch, "E110", {"start": v(13.3, 38.2) * mm, "end": v(13.3, 53.2) * mm});
            skLineSegment(sketch, "E111", {"start": v(13.3, 53.2) * mm, "end": v(28.15, 53.2) * mm});
            skArc(sketch, "E112", {"start": v(26.11, -7.38) * mm, "mid": v(26.87, -8.69) * mm, "end": v(28.28, -9.2) * mm});
            skArc(sketch, "E113", {"start": v(41.72, -9.2) * mm, "mid": v(43.13, -8.69) * mm, "end": v(43.89, -7.38) * mm});
            skLineSegment(sketch, "E114", {"start": v(45.33, 0.8) * mm, "end": v(51.2, 0.8) * mm});
            skLineSegment(sketch, "E115", {"start": v(51.2, 0.8) * mm, "end": v(51.2, 40.19) * mm});
            skLineSegment(sketch, "E116", {"start": v(-59.2, 0.8) * mm, "end": v(-59.2, 10.2) * mm});
            skLineSegment(sketch, "E117", {"start": v(-59.2, 10.2) * mm, "end": v(-51.2, 10.2) * mm});
            skLineSegment(sketch, "E118", {"start": v(-51.2, 10.2) * mm, "end": v(-51.2, 40.19) * mm});
            skArc(sketch, "E119", {"start": v(51.2, 40.19) * mm, "mid": v(40.2, 47.63) * mm, "end": v(28.15, 53.2) * mm});
            skArc(sketch, "E120", {"start": v(-28.15, 53.2) * mm, "mid": v(-40.2, 47.63) * mm, "end": v(-51.2, 40.19) * mm});
            skSolve(sketch);
        }
        {
            var Q0;
            Q0 = qSketchRegion(id + "F34", true);
            extrude(context, id + "F35", {"entities" : qUnion([Q0]), "operationType" : NewBodyOperationType.REMOVE, "depth" : 5 * mm});
        }
        {
            var Q0;
            Q0=makeQuery(id+"F31.opExtrude","SWEPT_FACE",FACE,{"disambiguationData":[OSD([sQuery(id+"F30.wireOp",EDGE,"E70")])]});
            var sketch = newSketch(context, id + "F36", { "sketchPlane" : qUnion([Q0])});
            skLineSegment(sketch, "E121", {"start": v(-37, 4) * mm, "end": v(-37, 4) * mm});
            skLineSegment(sketch, "E122", {"start": v(-37, 4) * mm, "end": v(-15.8, 2) * mm});
            skLineSegment(sketch, "E123", {"start": v(-15.8, 2) * mm, "end": v(-15.8, 4) * mm});
            skLineSegment(sketch, "E124", {"start": v(-15.8, 4) * mm, "end": v(-37, 4) * mm});
            skSolve(sketch);
        }
        {
            var Q0;
            Q0 = qSketchRegion(id + "F36", true);
            extrude(context, id + "F37", {"entities" : qUnion([Q0]), "operationType" : NewBodyOperationType.REMOVE, "oppositeDirection" : true, "depth" : 19 * mm});
        }
        {
            var Q0;
            Q0=makeQuery(id+"F31.opExtrude","SWEPT_FACE",FACE,{"disambiguationData":[OSD([sQuery(id+"F30.wireOp",EDGE,"E76")])]});
            var sketch = newSketch(context, id + "F38", { "sketchPlane" : qUnion([Q0])});
            skLineSegment(sketch, "E125", {"start": v(37, 4) * mm, "end": v(15.8, 2) * mm});
            skLineSegment(sketch, "E126", {"start": v(15.8, 2) * mm, "end": v(15.8, 4.3) * mm});
            skLineSegment(sketch, "E127", {"start": v(15.8, 4.3) * mm, "end": v(37, 4) * mm});
            skLineSegment(sketch, "E128", {"start": v(37, 4) * mm, "end": v(37, 4) * mm});
            skSolve(sketch);
        }
        {
            var Q0;
            Q0 = qSketchRegion(id + "F38", true);
            extrude(context, id + "F39", {"entities" : qUnion([Q0]), "operationType" : NewBodyOperationType.REMOVE, "oppositeDirection" : true, "depth" : 19 * mm});
        }
        {
            var Q0;
            Q0=makeQuery(id+"F37.boolean.opBoolean","INTERSECT",EDGE,{"derivedFrom":[makeQuery(id+"F31.opExtrude","SWEPT_FACE",FACE,{"disambiguationData":[OSD([sQuery(id+"F30.wireOp",EDGE,"E71")])]}),makeQuery(id+"F37.opExtrude","SWEPT_FACE",FACE,{"disambiguationData":[OSD([sQuery(id+"F36.wireOp",EDGE,"E122")])]})]});
            fillet(context, id + "F40", {"entities" : qUnion([Q0]), "radius" : 1 * mm, "tangentPropagation" : true, "allowEdgeOverflow" : false});
        }
        {
            var Q0;
            Q0=makeQuery(id+"F39.boolean.opBoolean","INTERSECT",EDGE,{"derivedFrom":[makeQuery(id+"F31.opExtrude","SWEPT_FACE",FACE,{"disambiguationData":[OSD([sQuery(id+"F30.wireOp",EDGE,"E79")])]}),makeQuery(id+"F39.opExtrude","SWEPT_FACE",FACE,{"disambiguationData":[OSD([sQuery(id+"F38.wireOp",EDGE,"E125")])]})]});
            fillet(context, id + "F41", {"entities" : qUnion([Q0]), "radius" : 1 * mm, "tangentPropagation" : true, "allowEdgeOverflow" : false});
        }
        {
            var Q0;
            Q0=makeQuery(id+"F25.opLoft","SWEPT_EDGE",EDGE,{"disambiguationData":[OSD([sQuery(id+"F23.wireOp",EDGE,"E62.top"),sQuery(id+"F23.wireOp",EDGE,"E62.left"),sQuery(id+"F24.wireOp",EDGE,"E64.bottom"),sQuery(id+"F24.wireOp",EDGE,"E64.left")])]});
            var Q1;
            Q1=makeQuery(id+"F25.opLoft","SWEPT_EDGE",EDGE,{"disambiguationData":[OSD([sQuery(id+"F23.wireOp",EDGE,"E62.top"),sQuery(id+"F23.wireOp",EDGE,"E62.right"),sQuery(id+"F24.wireOp",EDGE,"E64.bottom"),sQuery(id+"F24.wireOp",EDGE,"E64.right")])]});
            fillet(context, id + "F42", {"entities" : qUnion([Q0, Q1]), "radius" : 1 * mm, "tangentPropagation" : true, "allowEdgeOverflow" : false});
        }
        {
            var Q0;
            Q0=makeQuery(id+"F1.opExtrude","SWEPT_FACE",FACE,{"disambiguationData":[OSD([sQuery(id+"F0.wireOp",EDGE,"E6")])]});
            var sketch = newSketch(context, id + "F43", { "sketchPlane" : qUnion([Q0])});
            skLineSegment(sketch, "E129.bottom", {"start": v(-23, 3) * mm, "end": v(-26, 3) * mm});
            skLineSegment(sketch, "E129.top", {"start": v(-23, 0) * mm, "end": v(-26, 0) * mm});
            skLineSegment(sketch, "E129.left", {"start": v(-23, 3) * mm, "end": v(-23, 0) * mm});
            skLineSegment(sketch, "E129.right", {"start": v(-26, 3) * mm, "end": v(-26, 0) * mm});
            skLineSegment(sketch, "E130.bottom", {"start": v(-29, 3) * mm, "end": v(-32, 3) * mm});
            skLineSegment(sketch, "E130.top", {"start": v(-29, 0) * mm, "end": v(-32, 0) * mm});
            skLineSegment(sketch, "E130.left", {"start": v(-29, 3) * mm, "end": v(-29, 0) * mm});
            skLineSegment(sketch, "E130.right", {"start": v(-32, 3) * mm, "end": v(-32, 0) * mm});
            skSolve(sketch);
        }
        {
            var Q0;
            Q0 = qSketchRegion(id + "F43", true);
            extrude(context, id + "F44", {"entities" : qUnion([Q0]), "operationType" : NewBodyOperationType.REMOVE, "oppositeDirection" : true, "depth" : 6 * mm});
        }
        {
            var Q0;
            Q0=makeQuery(id+"F1.opExtrude","SWEPT_FACE",FACE,{"disambiguationData":[OSD([sQuery(id+"F0.wireOp",EDGE,"E3")])]});
            var sketch = newSketch(context, id + "F45", { "sketchPlane" : qUnion([Q0])});
            skLineSegment(sketch, "E131.bottom", {"start": v(23, 3) * mm, "end": v(26, 3) * mm});
            skLineSegment(sketch, "E131.top", {"start": v(23, 0) * mm, "end": v(26, 0) * mm});
            skLineSegment(sketch, "E131.left", {"start": v(23, 3) * mm, "end": v(23, 0) * mm});
            skLineSegment(sketch, "E131.right", {"start": v(26, 3) * mm, "end": v(26, 0) * mm});
            skLineSegment(sketch, "E132.bottom", {"start": v(29, 3) * mm, "end": v(32, 3) * mm});
            skLineSegment(sketch, "E132.top", {"start": v(29, 0) * mm, "end": v(32, 0) * mm});
            skLineSegment(sketch, "E132.left", {"start": v(29, 3) * mm, "end": v(29, 0) * mm});
            skLineSegment(sketch, "E132.right", {"start": v(32, 3) * mm, "end": v(32, 0) * mm});
            skSolve(sketch);
        }
        {
            var Q0;
            Q0 = qSketchRegion(id + "F45", true);
            extrude(context, id + "F46", {"entities" : qUnion([Q0]), "operationType" : NewBodyOperationType.REMOVE, "oppositeDirection" : true, "depth" : 6 * mm});
        }
    });
